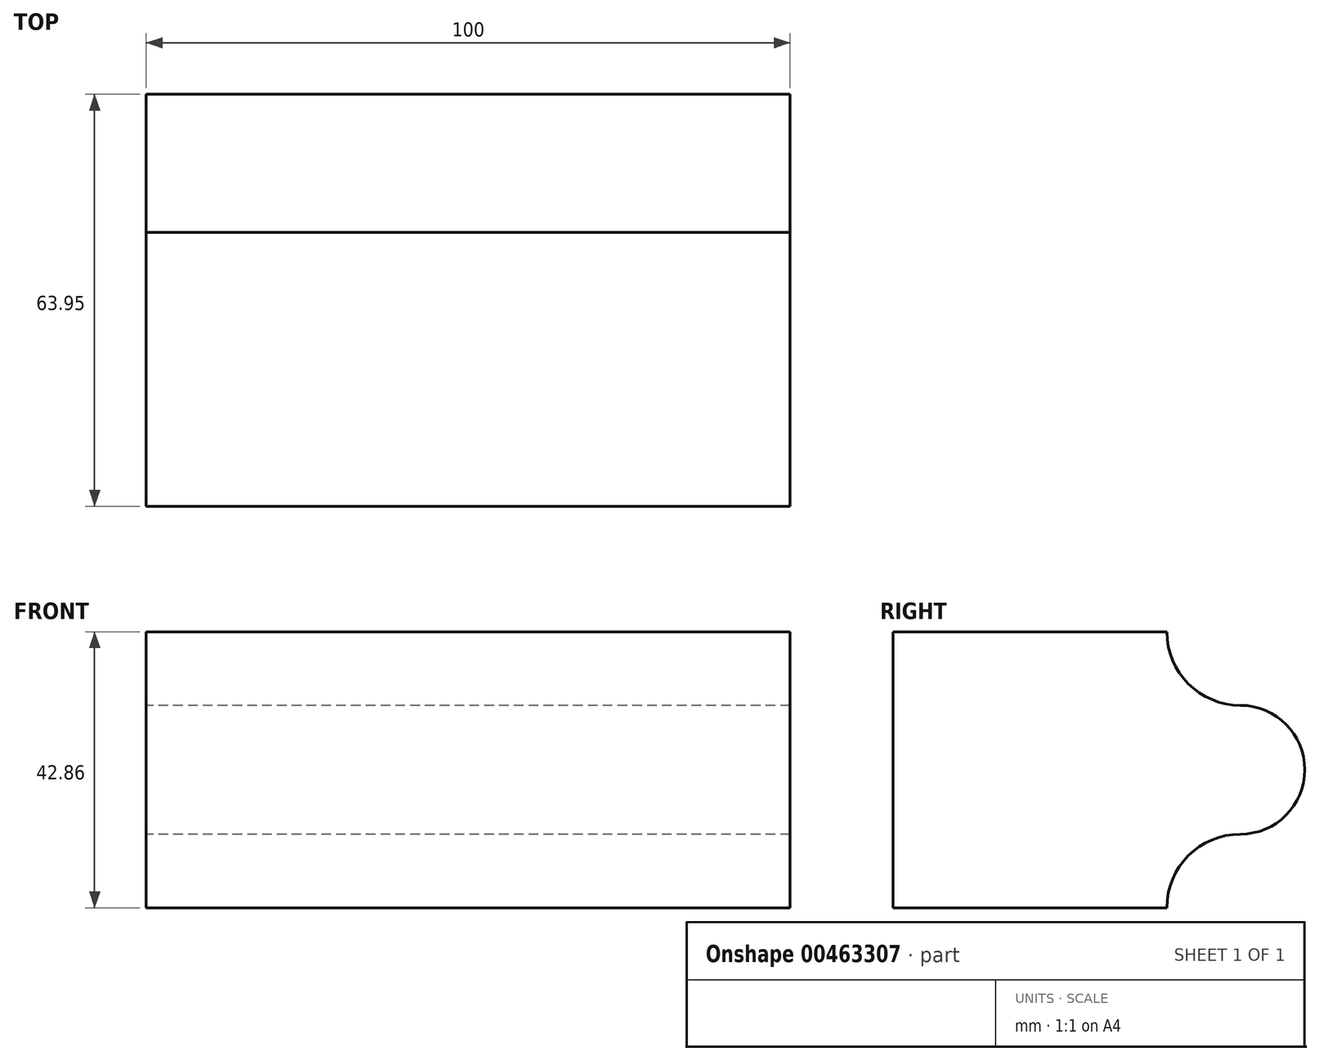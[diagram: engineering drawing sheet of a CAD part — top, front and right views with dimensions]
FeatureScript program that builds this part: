
annotation { "Feature Type Name" : "Feature", "Feature Type Description" : "" }
export const myFeature = defineFeature(function(context is Context, id is Id, definition is map)
    precondition{}
    {
        {
            var Q0;
            Q0=qCreatedBy(makeId("Right.planeOp"),FACE);
            var sketch = newSketch(context, id + "F0", { "sketchPlane" : qUnion([Q0])});
            skLineSegment(sketch, "E0", {"start": v(-53.95, 21.43) * mm, "end": v(-11.43, 21.43) * mm});
            skArc(sketch, "E1", {"start": v(-11.43, 21.43) * mm, "mid": v(-8.09, 13.35) * mm, "end": v(0, 10) * mm});
            skArc(sketch, "E2", {"start": v(0, -10) * mm, "mid": v(10, 0) * mm, "end": v(0, 10) * mm});
            skArc(sketch, "E3", {"start": v(0, -10) * mm, "mid": v(-8.09, -13.35) * mm, "end": v(-11.43, -21.43) * mm});
            skLineSegment(sketch, "E4", {"start": v(-11.43, -21.43) * mm, "end": v(-53.95, -21.43) * mm});
            skLineSegment(sketch, "E5", {"start": v(-53.95, -21.43) * mm, "end": v(-53.95, 21.43) * mm});
            skSolve(sketch);
        }
        {
            var Q0;
            Q0 = qSketchRegion(id + "F0", true);
            extrude(context, id + "F1", {"entities" : qUnion([Q0]), "endBound" : BoundingType.SYMMETRIC, "depth" : 100 * mm});
        }
    });
